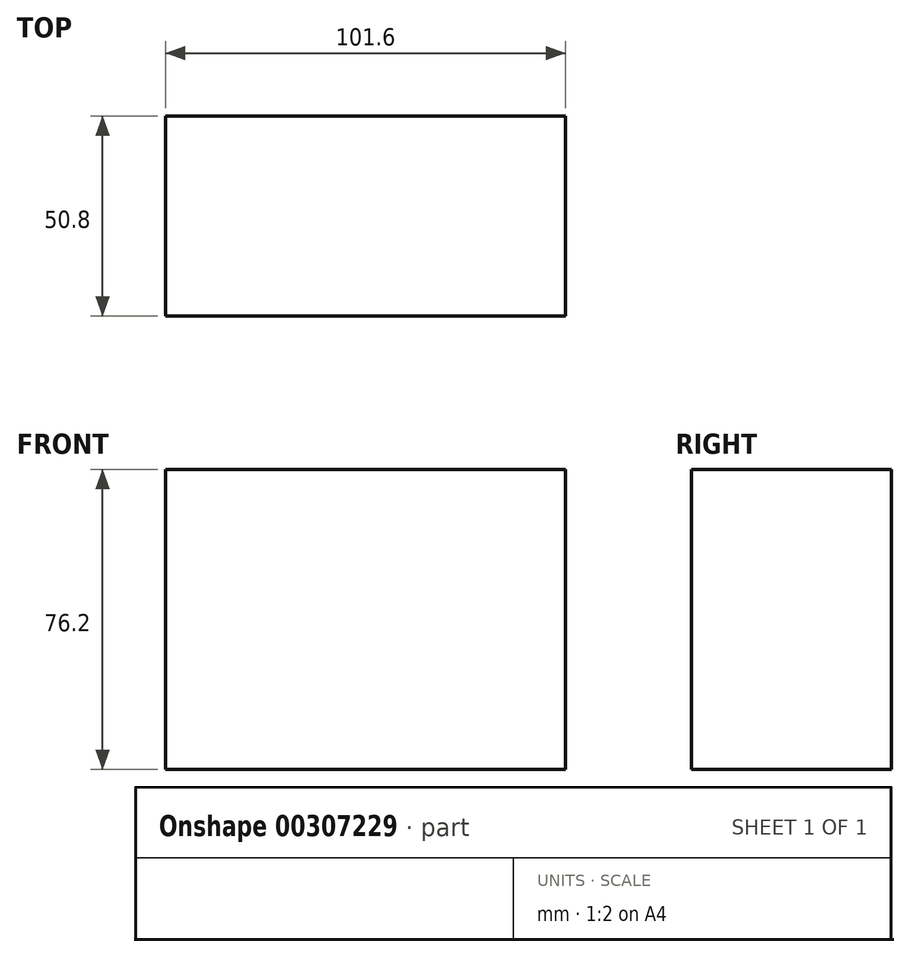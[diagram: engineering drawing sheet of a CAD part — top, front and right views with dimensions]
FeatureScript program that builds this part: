
annotation { "Feature Type Name" : "Feature", "Feature Type Description" : "" }
export const myFeature = defineFeature(function(context is Context, id is Id, definition is map)
    precondition{}
    {
        {
            var Q0;
            Q0=qCreatedBy(makeId("Front.planeOp"),FACE);
            var sketch = newSketch(context, id + "F0", { "sketchPlane" : qUnion([Q0])});
            skLineSegment(sketch, "E0", {"start": v(-51.46, 27.25) * mm, "end": v(-51.46, -48.95) * mm});
            skLineSegment(sketch, "E1", {"start": v(-51.46, -48.95) * mm, "end": v(50.14, -48.95) * mm});
            skLineSegment(sketch, "E2", {"start": v(50.14, -48.95) * mm, "end": v(50.14, 27.25) * mm});
            skLineSegment(sketch, "E3", {"start": v(50.14, 27.25) * mm, "end": v(-51.46, 27.25) * mm});
            skSolve(sketch);
        }
        {
            var Q0;
            Q0=makeQuery(id+"F0.imprint","IMPRINT",FACE,{"disambiguationData":[TD([[makeQuery(id+"F0.imprint","IMPRINT",EDGE,{"derivedFrom":sQuery(id+"F0.wireOp",EDGE,"E0")}),1.0]])]});
            extrude(context, id + "F1", {"entities" : qUnion([Q0]), "depth" : 50.8 * mm});
        }
        {
            var Q0;
            Q0=makeQuery(id+"F1.opExtrude","CAP_FACE",FACE,{"disambiguationData":[OSD([sQuery(id+"F0.wireOp",EDGE,"E0"),sQuery(id+"F0.wireOp",EDGE,"E1"),sQuery(id+"F0.wireOp",EDGE,"E2"),sQuery(id+"F0.wireOp",EDGE,"E3")])],"isStart":false});
            var sketch = newSketch(context, id + "F2", { "sketchPlane" : qUnion([Q0])});
            skLineSegment(sketch, "E4", {"start": v(-9, 27.25) * mm, "end": v(-31.42, -48.95) * mm});
            skLineSegment(sketch, "E5", {"start": v(50.14, -10.85) * mm, "end": v(25.27, -48.95) * mm});
            skLineSegment(sketch, "E6", {"start": v(-31.42, -48.95) * mm, "end": v(25.27, -48.95) * mm});
            skLineSegment(sketch, "E7", {"start": v(-9, 27.25) * mm, "end": v(50.14, 27.25) * mm});
            skLineSegment(sketch, "E8", {"start": v(50.14, 27.25) * mm, "end": v(50.14, -10.85) * mm});
            skSolve(sketch);
        }
        {
            var Q0;
            Q0=makeQuery(id+"F2.imprint","IMPRINT",FACE,{"disambiguationData":[TD([[makeQuery(id+"F2.imprint","IMPRINT",EDGE,{"derivedFrom":sQuery(id+"F2.wireOp",EDGE,"E4")}),1.0]])]});
            extrude(context, id + "F3", {"entities" : qUnion([Q0]), "operationType" : NewBodyOperationType.ADD, "oppositeDirection" : true, "depth" : 25.4 * mm});
        }
    });
